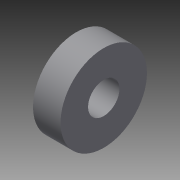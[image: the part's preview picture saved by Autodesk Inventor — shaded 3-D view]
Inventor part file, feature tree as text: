
AUTODESK INVENTOR PART (.ipt)
format: ipt  version: 2015 (Build 190159000, 159)  size: 99,328 bytes
history: native  units: mm
features: extrude x1, sketch x1
ambient origin geometry x8: Origin, YZ Plane, XZ Plane, XY Plane, X Axis, Y Axis, Z Axis, Center Point
bodies: Solid1 (feature_tree)
feature tree (2):
  extrude  "Extrusion1"  Depth=7.0mm
  sketch  "Sketch1"  dims[d0=8.0mm d1=22.0mm d2=7.0mm d3=0.0mm]
